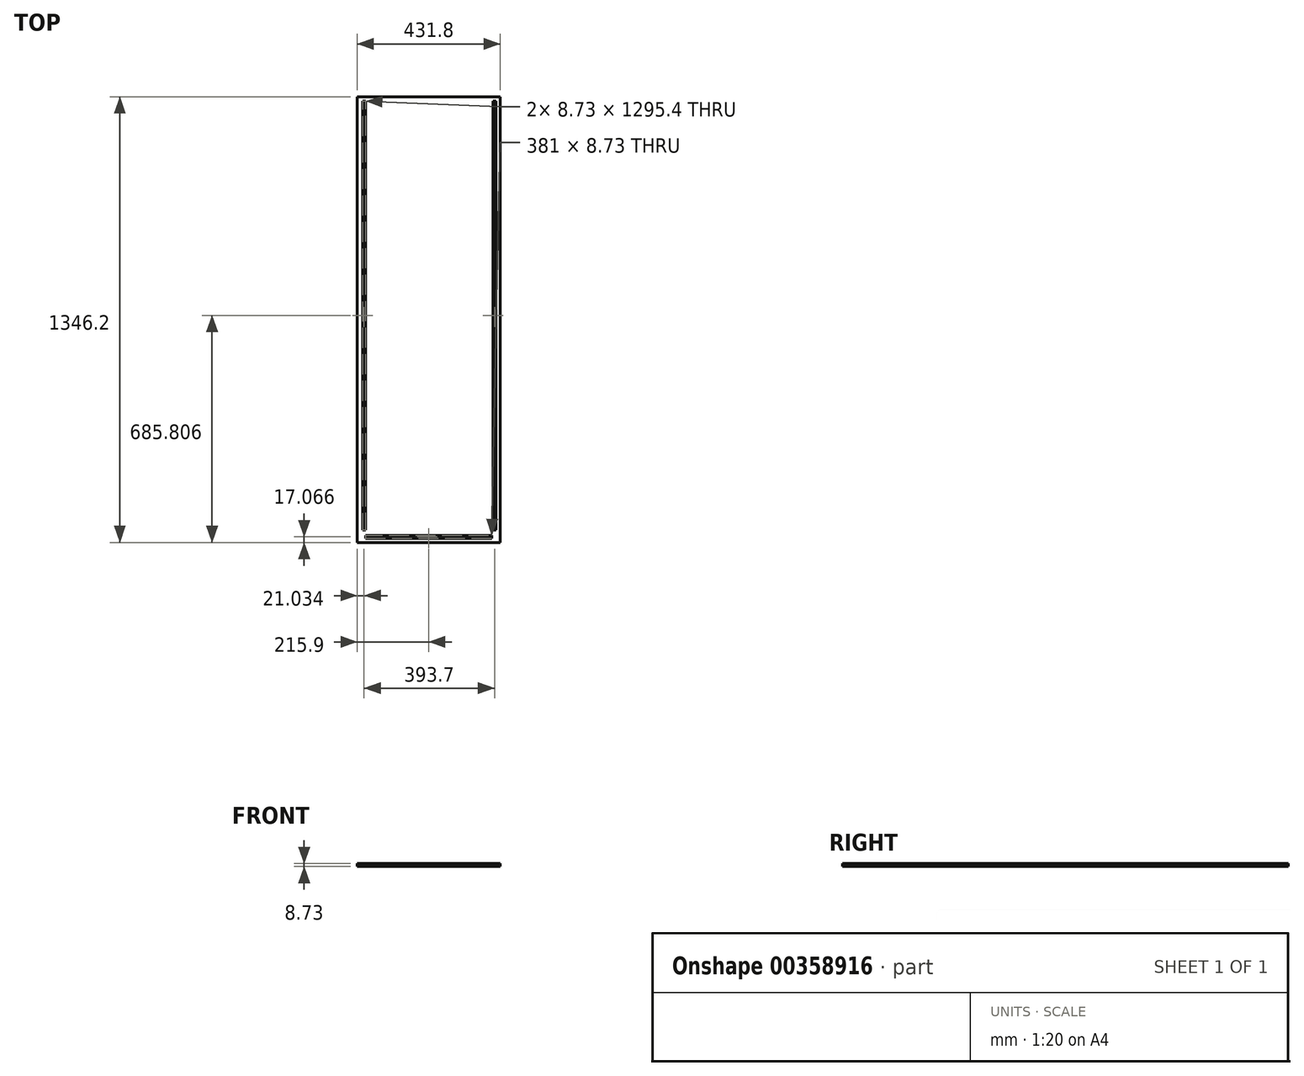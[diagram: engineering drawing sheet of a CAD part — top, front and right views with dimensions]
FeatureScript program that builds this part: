
annotation { "Feature Type Name" : "Feature", "Feature Type Description" : "" }
export const myFeature = defineFeature(function(context is Context, id is Id, definition is map)
    precondition{}
    {
        {
            var Q0;
            Q0=qCreatedBy(makeId("Top.planeOp"),FACE);
            var sketch = newSketch(context, id + "F0", { "sketchPlane" : qUnion([Q0])});
            skLineSegment(sketch, "E0.bottom", {"start": v(-215.9, 673.1) * mm, "end": v(215.9, 673.1) * mm});
            skLineSegment(sketch, "E0.top", {"start": v(-215.9, -673.1) * mm, "end": v(215.9, -673.1) * mm});
            skLineSegment(sketch, "E0.left", {"start": v(-215.9, 673.1) * mm, "end": v(-215.9, -673.1) * mm});
            skLineSegment(sketch, "E0.right", {"start": v(215.9, 673.1) * mm, "end": v(215.9, -673.1) * mm});
            skPoint(sketch, "E0.middle", {"position": v(0, 0) * mm});
            skLineSegment(sketch, "E1", {"start": v(0, -673.1) * mm, "end": v(0, -660.4) * mm});
            skPoint(sketch, "E1.endSnap0", {"position": v(0, -673.1) * mm});
            skLineSegment(sketch, "E2", {"start": v(0, -660.4) * mm, "end": v(190.5, -660.4) * mm});
            skLineSegment(sketch, "E3", {"start": v(0, -660.4) * mm, "end": v(-190.5, -660.4) * mm});
            skLineSegment(sketch, "E4", {"start": v(-190.5, -660.4) * mm, "end": v(-190.5, -651.67) * mm});
            skLineSegment(sketch, "E5", {"start": v(-190.5, -651.67) * mm, "end": v(190.5, -651.67) * mm});
            skLineSegment(sketch, "E6", {"start": v(190.5, -651.67) * mm, "end": v(190.5, -660.4) * mm});
            skLineSegment(sketch, "E7", {"start": v(215.9, 74.26) * mm, "end": v(203.2, 74.26) * mm});
            skLineSegment(sketch, "E8", {"start": v(-199.23, 660.4) * mm, "end": v(-199.23, -635) * mm});
            skLineSegment(sketch, "E9", {"start": v(203.2, 660.4) * mm, "end": v(203.2, -635) * mm});
            skLineSegment(sketch, "E10", {"start": v(-199.23, 660.4) * mm, "end": v(-190.5, 660.4) * mm});
            skLineSegment(sketch, "E11", {"start": v(203.2, 660.4) * mm, "end": v(194.47, 660.4) * mm});
            skLineSegment(sketch, "E12", {"start": v(-190.5, 660.4) * mm, "end": v(-190.5, -635) * mm});
            skLineSegment(sketch, "E13", {"start": v(-190.5, -635) * mm, "end": v(-199.23, -635) * mm});
            skLineSegment(sketch, "E14", {"start": v(194.47, 660.4) * mm, "end": v(194.47, -635) * mm});
            skLineSegment(sketch, "E15", {"start": v(194.47, -635) * mm, "end": v(203.2, -635) * mm});
            skSolve(sketch);
        }
        {
            var Q0;
            Q0=makeQuery(id+"F0.imprint","IMPRINT",FACE,{"disambiguationData":[TD([[makeQuery(id+"F0.imprint","IMPRINT",EDGE,{"derivedFrom":sQuery(id+"F0.wireOp",EDGE,"E0.bottom")}),-1.0]])]});
            extrude(context, id + "F1", {"entities" : qUnion([Q0]), "depth" : 8.73 * mm});
        }
    });
